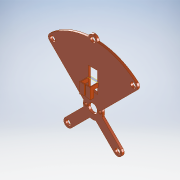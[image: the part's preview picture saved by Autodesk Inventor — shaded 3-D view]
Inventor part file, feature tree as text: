
AUTODESK INVENTOR PART (.ipt)
format: ipt  version: 2018.2 (Build 222227000, 227)  size: 244,736 bytes
history: native  units: mm
features: extrude x3, sketch x2, chamfer x1, plane x1, projected_geometry x1
ambient origin geometry x8: Origin, YZ Plane, XZ Plane, XY Plane, X Axis, Y Axis, Z Axis, Center Point
bodies: Body1 (feature_tree)
feature tree (8):
  extrude  "Extrusion11"  Depth=0.15mm
  chamfer  "Chamfer1"  Distance=8.0mm
  plane  "Work Plane5"
  extrude  "Extrusion12"  Depth=8.0mm
  extrude  "Extrusion13"  Depth=1.5mm
  sketch  "Sketch9"  dims[d0=10.0mm d1=0.15mm]
  projected_geometry  "Projected Loop1"
  sketch  "Sketch10"  dims[d2=2.5mm d4=8.0mm d5=8.0mm d14=2.0mm d15=6.0mm d16=45.0deg d47=10.0mm d48=11.0mm d56=0.15mm d57=0.15mm d58=24.0mm d61=45.0deg d62=40.0mm d63=5.0mm d64=6.0mm d69=45.0deg d70=65.0mm d71=6.0mm d72=5.0mm d104=22.0mm d105=4.0mm d106=6.0mm d108=17.0mm d111=2.5mm d112=0.0mm d113=0.5mm d114=2.0mm d115=45.0deg d116=12.0mm d117=1.5mm d118=10.0mm d119=5.0mm d121=1.0mm d122=1.0mm d125=12.2mm d126=2.5mm d127=0.0mm d128=8.0mm d129=5.0mm d130=2.5mm d131=0.0mm d132=10.0mm d133=1.5mm]
